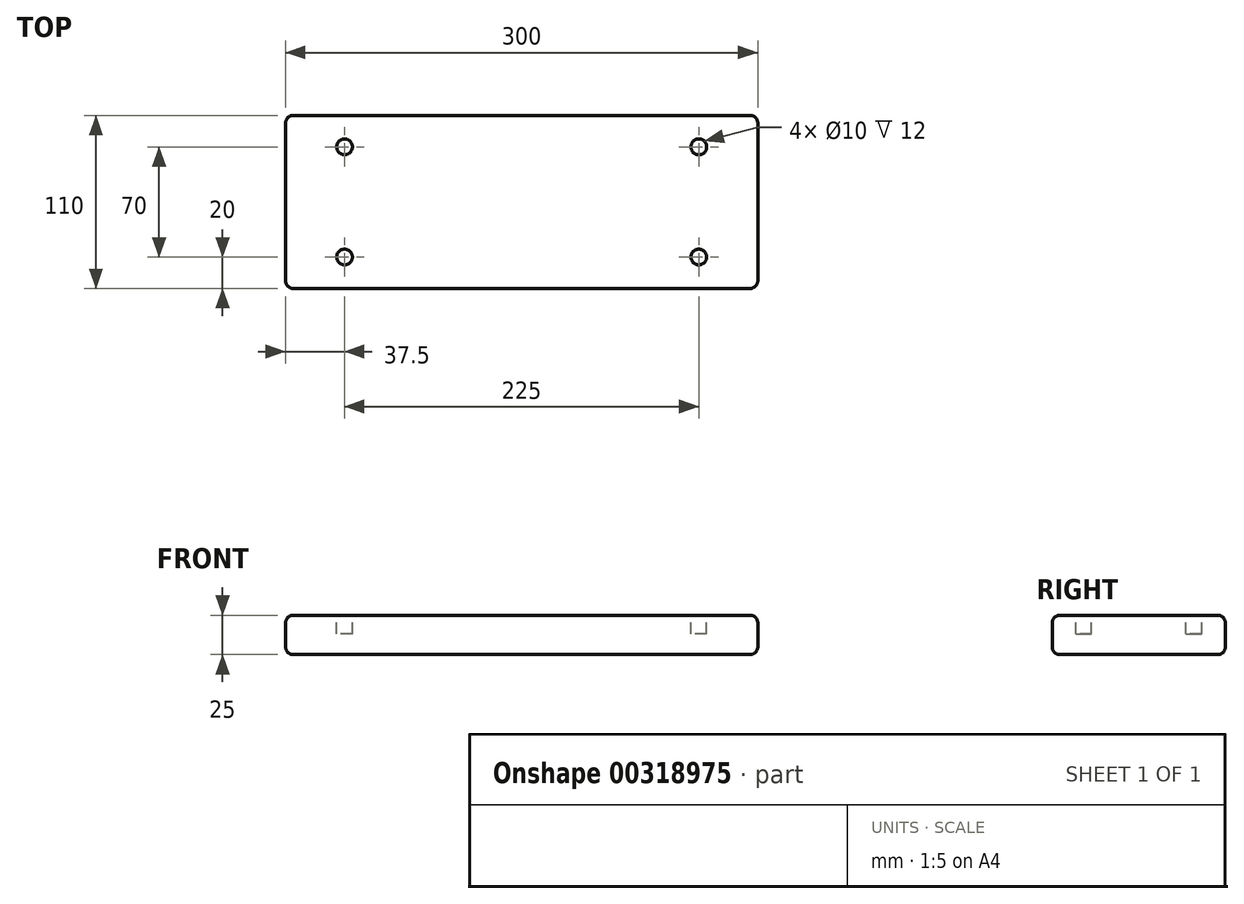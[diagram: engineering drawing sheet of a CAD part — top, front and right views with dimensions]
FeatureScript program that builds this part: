
annotation { "Feature Type Name" : "Feature", "Feature Type Description" : "" }
export const myFeature = defineFeature(function(context is Context, id is Id, definition is map)
    precondition{}
    {
        {
            var Q0;
            Q0=qCreatedBy(makeId("Top.planeOp"),FACE);
            var sketch = newSketch(context, id + "F0", { "sketchPlane" : qUnion([Q0])});
            skLineSegment(sketch, "E0.bottom", {"start": v(0, 0) * mm, "end": v(-300, 0) * mm});
            skLineSegment(sketch, "E0.top", {"start": v(0, 110) * mm, "end": v(-300, 110) * mm});
            skLineSegment(sketch, "E0.left", {"start": v(0, 0) * mm, "end": v(0, 110) * mm});
            skLineSegment(sketch, "E0.right", {"start": v(-300, 0) * mm, "end": v(-300, 110) * mm});
            skSolve(sketch);
        }
        {
            var Q0;
            Q0=qSketchRegion(id+"F0",true);
            extrude(context, id + "F1", {"entities" : qUnion([Q0]), "depth" : 25 * mm});
        }
        {
            var Q0;
            Q0=makeQuery(id+"F1.opExtrude","CAP_FACE",FACE,{"disambiguationData":[OSD([sQuery(id+"F0.wireOp",EDGE,"E0.bottom"),sQuery(id+"F0.wireOp",EDGE,"E0.top"),sQuery(id+"F0.wireOp",EDGE,"E0.left"),sQuery(id+"F0.wireOp",EDGE,"E0.right")])],"isStart":false});
            var sketch = newSketch(context, id + "F2", { "sketchPlane" : qUnion([Q0])});
            skLineSegment(sketch, "E1", {"start": v(-300, 90) * mm, "end": v(-262.5, 90) * mm, "construction": true});
            skLineSegment(sketch, "E2", {"start": v(-262.5, 90) * mm, "end": v(-262.5, 110) * mm, "construction": true});
            skPoint(sketch, "E3.startSnap0", {"position": v(-150, 110) * mm});
            skPoint(sketch, "E3.endSnap0", {"position": v(-150, 0) * mm});
            skLineSegment(sketch, "E4", {"start": v(0, 55) * mm, "end": v(-339.05, 55) * mm, "construction": true});
            skPoint(sketch, "E4.endSnap0", {"position": v(0, 55) * mm});
            skCircle(sketch, "E5", {"center": v(-262.5, 90) * mm, "radius": 5 * mm});
            skCircle(sketch, "E6.MirrorC", {"center": v(-262.5, 20) * mm, "radius": 5 * mm});
            skLineSegment(sketch, "E7.MirrorCS", {"start": v(-150, -43.45) * mm, "end": v(-150, 152.33) * mm, "construction": true});
            skCircle(sketch, "E8.MirrorC", {"center": v(-37.5, 90) * mm, "radius": 5 * mm});
            skCircle(sketch, "E9.MirrorC", {"center": v(-37.5, 20) * mm, "radius": 5 * mm});
            skSolve(sketch);
        }
        {
            var Q0;
            Q0=qSketchRegion(id+"F2",true);
            extrude(context, id + "F3", {"entities" : qUnion([Q0]), "operationType" : NewBodyOperationType.REMOVE, "oppositeDirection" : true, "depth" : 12 * mm});
        }
        {
            var Q0;
            Q0=makeQuery(id+"F1.opExtrude","SWEPT_FACE",FACE,{"disambiguationData":[OSD([sQuery(id+"F0.wireOp",EDGE,"E0.top")])]});
            var Q1;
            Q1=makeQuery(id+"F1.opExtrude","SWEPT_FACE",FACE,{"disambiguationData":[OSD([sQuery(id+"F0.wireOp",EDGE,"E0.right")])]});
            var Q2;
            Q2=makeQuery(id+"F1.opExtrude","SWEPT_FACE",FACE,{"disambiguationData":[OSD([sQuery(id+"F0.wireOp",EDGE,"E0.bottom")])]});
            var Q3;
            Q3=makeQuery(id+"F1.opExtrude","SWEPT_FACE",FACE,{"disambiguationData":[OSD([sQuery(id+"F0.wireOp",EDGE,"E0.left")])]});
            fillet(context, id + "F4", {"entities" : qUnion([Q0, Q1, Q2, Q3]), "radius" : 5 * mm, "tangentPropagation" : true, "allowEdgeOverflow" : false});
        }
    });
